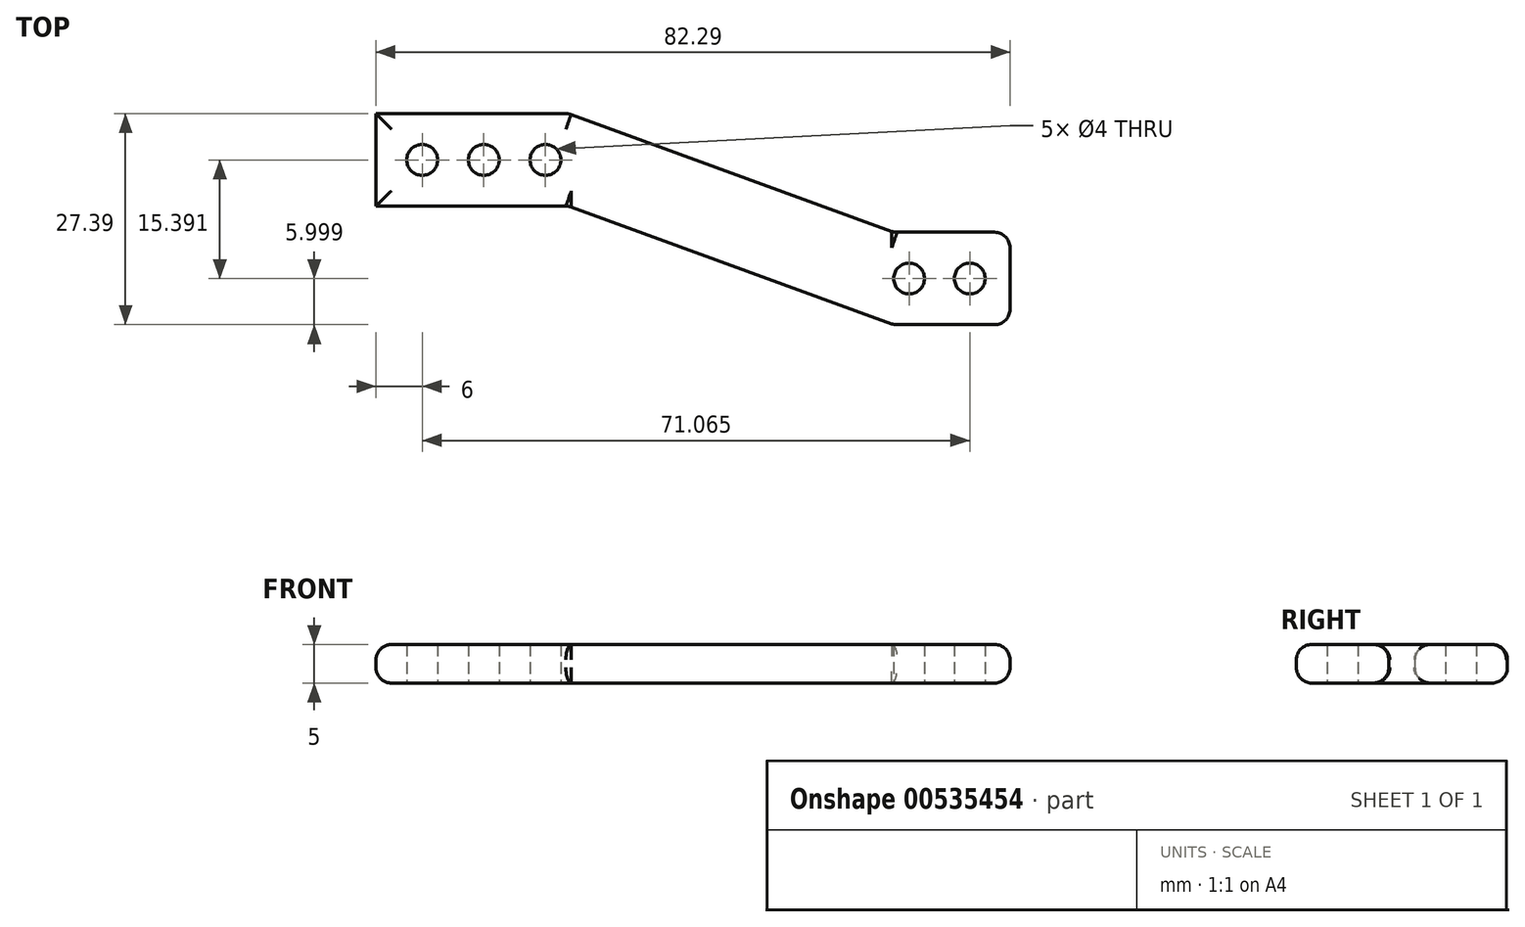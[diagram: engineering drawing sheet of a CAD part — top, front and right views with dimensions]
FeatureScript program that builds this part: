
annotation { "Feature Type Name" : "Feature", "Feature Type Description" : "" }
export const myFeature = defineFeature(function(context is Context, id is Id, definition is map)
    precondition{}
    {
        {
            var Q0;
            Q0=qCreatedBy(makeId("Top.planeOp"),FACE);
            var sketch = newSketch(context, id + "F0", { "sketchPlane" : qUnion([Q0])});
            skLineSegment(sketch, "E0.bottom", {"start": v(0, 0) * mm, "end": v(-25, 0) * mm});
            skLineSegment(sketch, "E0.top", {"start": v(0, 12) * mm, "end": v(-25, 12) * mm});
            skLineSegment(sketch, "E0.left", {"start": v(0, 0) * mm, "end": v(0, 12) * mm});
            skLineSegment(sketch, "E0.right", {"start": v(-25, 0) * mm, "end": v(-25, 12) * mm});
            skLineSegment(sketch, "E1", {"start": v(0, 0) * mm, "end": v(42.29, -15.4) * mm});
            skLineSegment(sketch, "E2", {"start": v(0, 12) * mm, "end": v(42.29, -3.4) * mm});
            skCircle(sketch, "E3", {"center": v(-19, 6) * mm, "radius": 2 * mm});
            skCircle(sketch, "E4", {"center": v(-3, 6) * mm, "radius": 2 * mm});
            skCircle(sketch, "E5", {"center": v(-11, 6) * mm, "radius": 2 * mm});
            skPoint(sketch, "E5.centerSnap0", {"position": v(-25, 6) * mm});
            skLineSegment(sketch, "E6.bottom", {"start": v(42.29, -3.4) * mm, "end": v(42.29, -3.4) * mm});
            skLineSegment(sketch, "E6.top", {"start": v(42.29, -15.4) * mm, "end": v(42.29, -15.4) * mm});
            skLineSegment(sketch, "E7.bottom", {"start": v(42.29, -3.4) * mm, "end": v(57.29, -3.4) * mm});
            skLineSegment(sketch, "E7.top", {"start": v(42.29, -15.4) * mm, "end": v(57.29, -15.4) * mm});
            skLineSegment(sketch, "E7.right", {"start": v(57.29, -3.4) * mm, "end": v(57.29, -15.4) * mm});
            skCircle(sketch, "E8", {"center": v(44.2, -9.4) * mm, "radius": 2 * mm});
            skPoint(sketch, "E8.centerSnap0", {"position": v(57.29, -9.4) * mm});
            skCircle(sketch, "E9", {"center": v(52.06, -9.4) * mm, "radius": 2 * mm});
            skSolve(sketch);
        }
        {
            var Q0;
            Q0 = qSketchRegion(id + "F0", true);
            extrude(context, id + "F1", {"entities" : qUnion([Q0]), "depth" : 5 * mm, "offsetDistance" : 25 * mm});
        }
        {
            var Q0;
            Q0=makeQuery(id+"F1.opExtrude","CAP_EDGE",EDGE,{"disambiguationData":[OSD([sQuery(id+"F0.wireOp",EDGE,"E0.bottom")])],"isStart":true});
            var Q1;
            Q1=makeQuery(id+"F1.opExtrude","CAP_EDGE",EDGE,{"disambiguationData":[OSD([sQuery(id+"F0.wireOp",EDGE,"E0.right")])],"isStart":true});
            var Q2;
            Q2=makeQuery(id+"F1.opExtrude","CAP_EDGE",EDGE,{"disambiguationData":[OSD([sQuery(id+"F0.wireOp",EDGE,"E0.top")])],"isStart":true});
            var Q3;
            Q3=makeQuery(id+"F1.opExtrude","CAP_EDGE",EDGE,{"disambiguationData":[OSD([sQuery(id+"F0.wireOp",EDGE,"E2")])],"isStart":true});
            var Q4;
            Q4=makeQuery(id+"F1.opExtrude","CAP_EDGE",EDGE,{"disambiguationData":[OSD([sQuery(id+"F0.wireOp",EDGE,"E7.bottom")])],"isStart":true});
            var Q5;
            Q5=makeQuery(id+"F1.opExtrude","CAP_EDGE",EDGE,{"disambiguationData":[OSD([sQuery(id+"F0.wireOp",EDGE,"E7.right")])],"isStart":true});
            var Q6;
            Q6=makeQuery(id+"F1.opExtrude","CAP_EDGE",EDGE,{"disambiguationData":[OSD([sQuery(id+"F0.wireOp",EDGE,"E7.top")])],"isStart":true});
            var Q7;
            Q7=makeQuery(id+"F1.opExtrude","CAP_EDGE",EDGE,{"disambiguationData":[OSD([sQuery(id+"F0.wireOp",EDGE,"E1")])],"isStart":true});
            fillet(context, id + "F2", {"entities" : qUnion([Q0, Q1, Q2, Q3, Q4, Q5, Q6, Q7]), "radius" : 2 * mm, "tangentPropagation" : true, "allowEdgeOverflow" : false});
        }
        {
            var Q0;
            Q0=makeQuery(id+"F1.opExtrude","CAP_EDGE",EDGE,{"disambiguationData":[OSD([sQuery(id+"F0.wireOp",EDGE,"E7.right")])],"isStart":false});
            var Q1;
            Q1=makeQuery(id+"F1.opExtrude","CAP_EDGE",EDGE,{"disambiguationData":[OSD([sQuery(id+"F0.wireOp",EDGE,"E7.top")])],"isStart":false});
            var Q2;
            Q2=makeQuery(id+"F1.opExtrude","CAP_EDGE",EDGE,{"disambiguationData":[OSD([sQuery(id+"F0.wireOp",EDGE,"E1")])],"isStart":false});
            var Q3;
            Q3=makeQuery(id+"F1.opExtrude","CAP_EDGE",EDGE,{"disambiguationData":[OSD([sQuery(id+"F0.wireOp",EDGE,"E0.bottom")])],"isStart":false});
            var Q4;
            Q4=makeQuery(id+"F1.opExtrude","CAP_EDGE",EDGE,{"disambiguationData":[OSD([sQuery(id+"F0.wireOp",EDGE,"E0.right")])],"isStart":false});
            var Q5;
            Q5=makeQuery(id+"F1.opExtrude","CAP_EDGE",EDGE,{"disambiguationData":[OSD([sQuery(id+"F0.wireOp",EDGE,"E0.top")])],"isStart":false});
            var Q6;
            Q6=makeQuery(id+"F1.opExtrude","CAP_EDGE",EDGE,{"disambiguationData":[OSD([sQuery(id+"F0.wireOp",EDGE,"E2")])],"isStart":false});
            var Q7;
            Q7=makeQuery(id+"F1.opExtrude","CAP_EDGE",EDGE,{"disambiguationData":[OSD([sQuery(id+"F0.wireOp",EDGE,"E7.bottom")])],"isStart":false});
            fillet(context, id + "F3", {"entities" : qUnion([Q0, Q1, Q2, Q3, Q4, Q5, Q6, Q7]), "radius" : 2 * mm, "tangentPropagation" : true, "allowEdgeOverflow" : false});
        }
        {
            var Q0;
            Q0=makeQuery(id+"F3.opFillet","BLEND_EDGE",EDGE,{"blendedFrom":[makeQuery(id+"F1.opExtrude","CAP_EDGE",EDGE,{"disambiguationData":[OSD([sQuery(id+"F0.wireOp",EDGE,"E2")])],"isStart":false}),makeQuery(id+"F1.opExtrude","CAP_EDGE",EDGE,{"disambiguationData":[OSD([sQuery(id+"F0.wireOp",EDGE,"E7.bottom")])],"isStart":false})],"blendedInto":[]});
            var Q1;
            Q1=makeQuery(id+"F1.opExtrude","SWEPT_EDGE",EDGE,{"disambiguationData":[OSD([sQuery(id+"F0.wireOp",EDGE,"E2"),sQuery(id+"F0.wireOp",EDGE,"E7.bottom"),sQuery(id+"F0.wireOp",EDGE,"E7.left")])]});
            var Q2;
            Q2=makeQuery(id+"F2.opFillet","BLEND_EDGE",EDGE,{"blendedFrom":[makeQuery(id+"F1.opExtrude","CAP_EDGE",EDGE,{"disambiguationData":[OSD([sQuery(id+"F0.wireOp",EDGE,"E2")])],"isStart":true}),makeQuery(id+"F1.opExtrude","CAP_EDGE",EDGE,{"disambiguationData":[OSD([sQuery(id+"F0.wireOp",EDGE,"E7.bottom")])],"isStart":true})],"blendedInto":[]});
            fillet(context, id + "F4", {"entities" : qUnion([Q0, Q1, Q2]), "radius" : 2 * mm, "tangentPropagation" : true, "allowEdgeOverflow" : false});
        }
        {
            var Q0;
            Q0=makeQuery(id+"F3.opFillet","BLEND_EDGE",EDGE,{"blendedFrom":[makeQuery(id+"F1.opExtrude","CAP_EDGE",EDGE,{"disambiguationData":[OSD([sQuery(id+"F0.wireOp",EDGE,"E0.bottom")])],"isStart":false}),makeQuery(id+"F1.opExtrude","CAP_EDGE",EDGE,{"disambiguationData":[OSD([sQuery(id+"F0.wireOp",EDGE,"E1")])],"isStart":false})],"blendedInto":[]});
            var Q1;
            Q1=makeQuery(id+"F1.opExtrude","SWEPT_EDGE",EDGE,{"disambiguationData":[OSD([sQuery(id+"F0.wireOp",EDGE,"E0.bottom"),sQuery(id+"F0.wireOp",EDGE,"E0.left"),sQuery(id+"F0.wireOp",EDGE,"E1")])]});
            var Q2;
            Q2=makeQuery(id+"F2.opFillet","BLEND_EDGE",EDGE,{"blendedFrom":[makeQuery(id+"F1.opExtrude","CAP_EDGE",EDGE,{"disambiguationData":[OSD([sQuery(id+"F0.wireOp",EDGE,"E0.bottom")])],"isStart":true}),makeQuery(id+"F1.opExtrude","CAP_EDGE",EDGE,{"disambiguationData":[OSD([sQuery(id+"F0.wireOp",EDGE,"E1")])],"isStart":true})],"blendedInto":[]});
            fillet(context, id + "F5", {"entities" : qUnion([Q0, Q1, Q2]), "radius" : 2 * mm, "tangentPropagation" : true, "allowEdgeOverflow" : false});
        }
        {
            var Q0;
            Q0=makeQuery(id+"F3.opFillet","BLEND_EDGE",EDGE,{"blendedFrom":[makeQuery(id+"F1.opExtrude","CAP_EDGE",EDGE,{"disambiguationData":[OSD([sQuery(id+"F0.wireOp",EDGE,"E1")])],"isStart":false}),makeQuery(id+"F1.opExtrude","CAP_EDGE",EDGE,{"disambiguationData":[OSD([sQuery(id+"F0.wireOp",EDGE,"E7.top")])],"isStart":false})],"blendedInto":[]});
            var Q1;
            Q1=makeQuery(id+"F1.opExtrude","SWEPT_EDGE",EDGE,{"disambiguationData":[OSD([sQuery(id+"F0.wireOp",EDGE,"E1"),sQuery(id+"F0.wireOp",EDGE,"E7.top"),sQuery(id+"F0.wireOp",EDGE,"E7.left")])]});
            var Q2;
            Q2=makeQuery(id+"F2.opFillet","BLEND_EDGE",EDGE,{"blendedFrom":[makeQuery(id+"F1.opExtrude","CAP_EDGE",EDGE,{"disambiguationData":[OSD([sQuery(id+"F0.wireOp",EDGE,"E1")])],"isStart":true}),makeQuery(id+"F1.opExtrude","CAP_EDGE",EDGE,{"disambiguationData":[OSD([sQuery(id+"F0.wireOp",EDGE,"E7.top")])],"isStart":true})],"blendedInto":[]});
            var Q3;
            Q3=makeQuery(id+"F3.opFillet","BLEND_EDGE",EDGE,{"blendedFrom":[makeQuery(id+"F1.opExtrude","CAP_EDGE",EDGE,{"disambiguationData":[OSD([sQuery(id+"F0.wireOp",EDGE,"E7.top")])],"isStart":false}),makeQuery(id+"F1.opExtrude","CAP_EDGE",EDGE,{"disambiguationData":[OSD([sQuery(id+"F0.wireOp",EDGE,"E7.right")])],"isStart":false})],"blendedInto":[]});
            var Q4;
            Q4=makeQuery(id+"F1.opExtrude","SWEPT_EDGE",EDGE,{"disambiguationData":[OSD([sQuery(id+"F0.wireOp",EDGE,"E7.top"),sQuery(id+"F0.wireOp",EDGE,"E7.right")])]});
            var Q5;
            Q5=makeQuery(id+"F2.opFillet","BLEND_EDGE",EDGE,{"blendedFrom":[makeQuery(id+"F1.opExtrude","CAP_EDGE",EDGE,{"disambiguationData":[OSD([sQuery(id+"F0.wireOp",EDGE,"E7.top")])],"isStart":true}),makeQuery(id+"F1.opExtrude","CAP_EDGE",EDGE,{"disambiguationData":[OSD([sQuery(id+"F0.wireOp",EDGE,"E7.right")])],"isStart":true})],"blendedInto":[]});
            fillet(context, id + "F6", {"entities" : qUnion([Q0, Q1, Q2, Q3, Q4, Q5]), "radius" : 2 * mm, "tangentPropagation" : true, "allowEdgeOverflow" : false});
        }
        {
            var Q0;
            Q0=makeQuery(id+"F3.opFillet","BLEND_EDGE",EDGE,{"blendedFrom":[makeQuery(id+"F1.opExtrude","CAP_EDGE",EDGE,{"disambiguationData":[OSD([sQuery(id+"F0.wireOp",EDGE,"E7.bottom")])],"isStart":false}),makeQuery(id+"F1.opExtrude","CAP_EDGE",EDGE,{"disambiguationData":[OSD([sQuery(id+"F0.wireOp",EDGE,"E7.right")])],"isStart":false})],"blendedInto":[]});
            var Q1;
            Q1=makeQuery(id+"F1.opExtrude","SWEPT_EDGE",EDGE,{"disambiguationData":[OSD([sQuery(id+"F0.wireOp",EDGE,"E7.bottom"),sQuery(id+"F0.wireOp",EDGE,"E7.right")])]});
            var Q2;
            Q2=makeQuery(id+"F2.opFillet","BLEND_EDGE",EDGE,{"blendedFrom":[makeQuery(id+"F1.opExtrude","CAP_EDGE",EDGE,{"disambiguationData":[OSD([sQuery(id+"F0.wireOp",EDGE,"E7.bottom")])],"isStart":true}),makeQuery(id+"F1.opExtrude","CAP_EDGE",EDGE,{"disambiguationData":[OSD([sQuery(id+"F0.wireOp",EDGE,"E7.right")])],"isStart":true})],"blendedInto":[]});
            fillet(context, id + "F7", {"entities" : qUnion([Q0, Q1, Q2]), "radius" : 2 * mm, "tangentPropagation" : true, "allowEdgeOverflow" : false});
        }
        {
            var Q0;
            Q0=makeQuery(id+"F2.opFillet","BLEND_EDGE",EDGE,{"blendedFrom":[makeQuery(id+"F1.opExtrude","CAP_EDGE",EDGE,{"disambiguationData":[OSD([sQuery(id+"F0.wireOp",EDGE,"E0.top")])],"isStart":true}),makeQuery(id+"F1.opExtrude","CAP_EDGE",EDGE,{"disambiguationData":[OSD([sQuery(id+"F0.wireOp",EDGE,"E2")])],"isStart":true})],"blendedInto":[]});
            var Q1;
            Q1=makeQuery(id+"F3.opFillet","BLEND_EDGE",EDGE,{"blendedFrom":[makeQuery(id+"F1.opExtrude","CAP_EDGE",EDGE,{"disambiguationData":[OSD([sQuery(id+"F0.wireOp",EDGE,"E0.top")])],"isStart":false}),makeQuery(id+"F1.opExtrude","CAP_EDGE",EDGE,{"disambiguationData":[OSD([sQuery(id+"F0.wireOp",EDGE,"E2")])],"isStart":false})],"blendedInto":[]});
            var Q2;
            Q2=makeQuery(id+"F1.opExtrude","SWEPT_EDGE",EDGE,{"disambiguationData":[OSD([sQuery(id+"F0.wireOp",EDGE,"E0.top"),sQuery(id+"F0.wireOp",EDGE,"E0.left"),sQuery(id+"F0.wireOp",EDGE,"E2")])]});
            fillet(context, id + "F8", {"entities" : qUnion([Q0, Q1, Q2]), "radius" : 2 * mm, "tangentPropagation" : true, "allowEdgeOverflow" : false});
        }
    });
